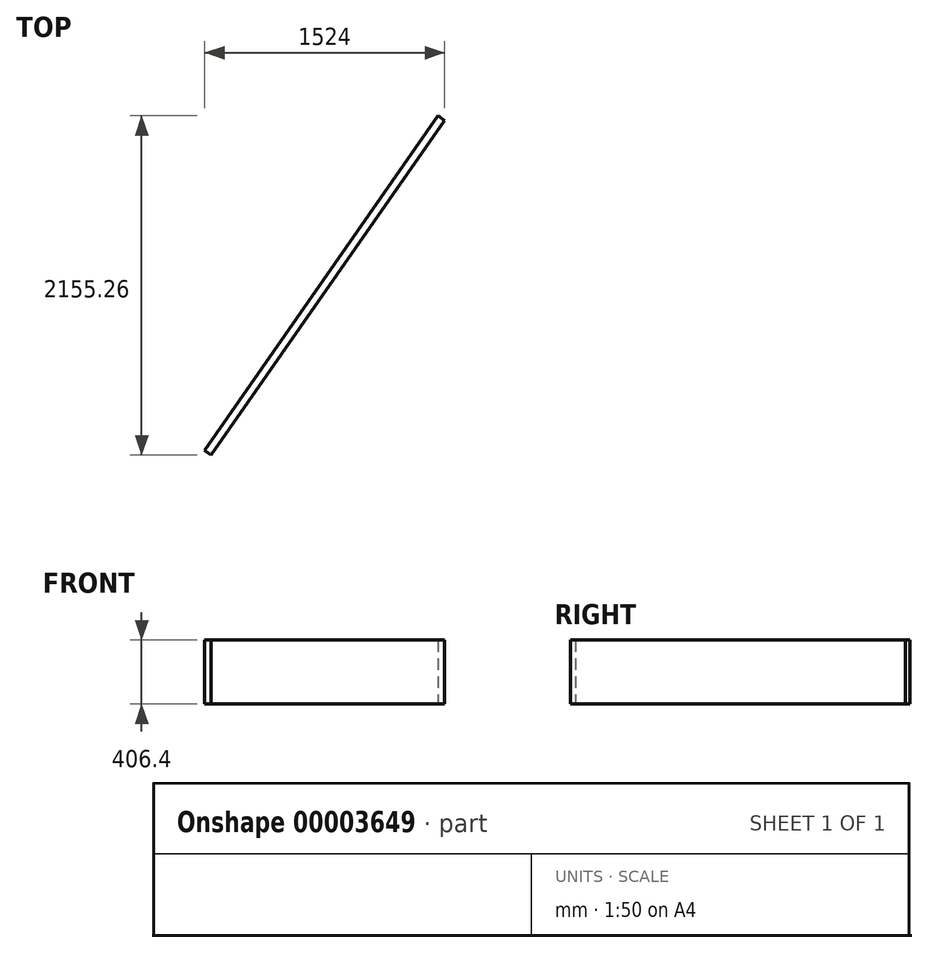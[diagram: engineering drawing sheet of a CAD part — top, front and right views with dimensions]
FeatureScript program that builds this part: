
annotation { "Feature Type Name" : "Feature", "Feature Type Description" : "" }
export const myFeature = defineFeature(function(context is Context, id is Id, definition is map)
    precondition{}
    {
        {
            var Q0;
            Q0=qCreatedBy(makeId("Top.planeOp"),FACE);
            var sketch = newSketch(context, id + "F0", { "sketchPlane" : qUnion([Q0])});
            skLineSegment(sketch, "E0.rect.bottom", {"start": v(762, 1077.63) * mm, "end": v(-762, 1077.63) * mm});
            skLineSegment(sketch, "E0.rect.top", {"start": v(762, -1077.63) * mm, "end": v(-762, -1077.63) * mm});
            skLineSegment(sketch, "E0.rect.left", {"start": v(762, 1077.63) * mm, "end": v(762, -1077.63) * mm});
            skLineSegment(sketch, "E0.rect.right", {"start": v(-762, 1077.63) * mm, "end": v(-762, -1077.63) * mm});
            skPoint(sketch, "E0.rect.middle", {"position": v(0, 0) * mm});
            skLineSegment(sketch, "E1", {"start": v(-762, -1048.3) * mm, "end": v(-720.52, -1077.63) * mm});
            skLineSegment(sketch, "E2", {"start": v(-720.52, -1077.63) * mm, "end": v(762, 1048.58) * mm});
            skLineSegment(sketch, "E3", {"start": v(762, 1048.58) * mm, "end": v(720.33, 1077.63) * mm});
            skLineSegment(sketch, "E4", {"start": v(720.33, 1077.63) * mm, "end": v(-762, -1048.3) * mm});
            skLineSegment(sketch, "E5", {"start": v(-762, -1077.63) * mm, "end": v(762, 1077.63) * mm, "construction": true});
            skSolve(sketch);
        }
        {
            var Q0;
            Q0=makeQuery(id+"F0.imprint","IMPRINT",FACE,{"disambiguationData":[TD([[makeQuery(id+"F0.imprint","IMPRINT",EDGE,{"derivedFrom":sQuery(id+"F0.wireOp",EDGE,"E1")}),1.0]])]});
            extrude(context, id + "F1", {"entities" : qUnion([Q0]), "depth" : 406.4 * mm});
        }
    });
